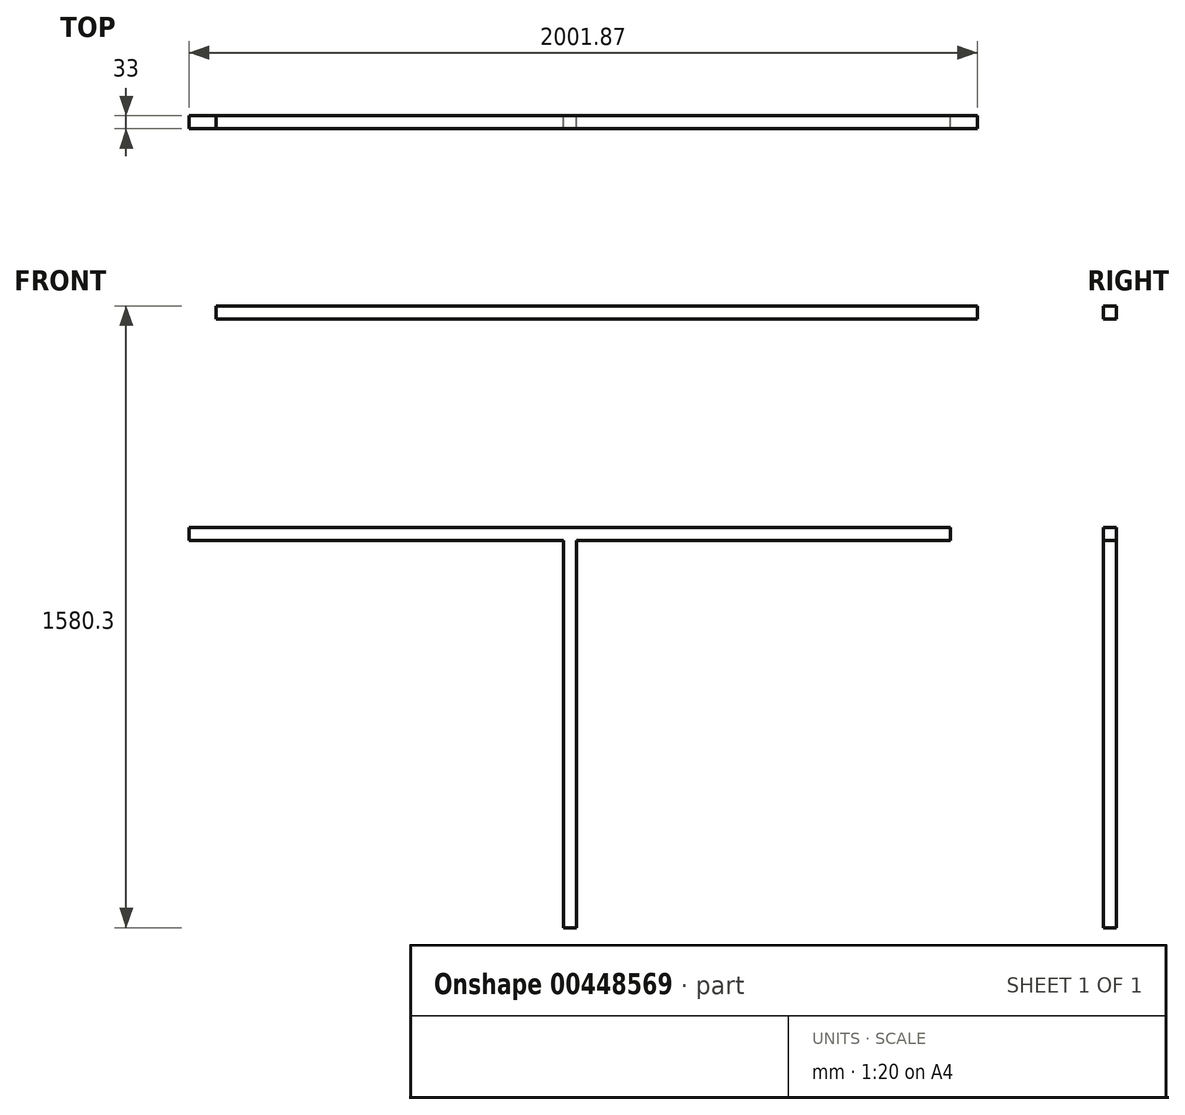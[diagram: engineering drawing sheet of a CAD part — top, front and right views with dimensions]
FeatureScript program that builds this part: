
annotation { "Feature Type Name" : "Feature", "Feature Type Description" : "" }
export const myFeature = defineFeature(function(context is Context, id is Id, definition is map)
    precondition{}
    {
        {
            var Q0;
            Q0=qCreatedBy(makeId("Front.planeOp"),FACE);
            var sketch = newSketch(context, id + "F0", { "sketchPlane" : qUnion([Q0])});
            skLineSegment(sketch, "E0.bottom", {"start": v(983.5, 0) * mm, "end": v(1016.5, 0) * mm});
            skLineSegment(sketch, "E1.0", {"start": v(33, 983.5) * mm, "end": v(33, 1016.5) * mm});
            skLineSegment(sketch, "E1.2", {"start": v(1967, 983.5) * mm, "end": v(1967, 1016.5) * mm});
            skLineSegment(sketch, "E2.right", {"start": v(1016.5, 983.5) * mm, "end": v(1016.5, 0) * mm});
            skLineSegment(sketch, "E3.bottom", {"start": v(33, 1016.5) * mm, "end": v(1967, 1016.5) * mm});
            skLineSegment(sketch, "E3.top", {"start": v(33, 983.5) * mm, "end": v(983.5, 983.5) * mm});
            skLineSegment(sketch, "E3.left", {"start": v(33, 1016.5) * mm, "end": v(33, 983.5) * mm});
            skLineSegment(sketch, "E3.right", {"start": v(1967, 1016.5) * mm, "end": v(1967, 983.5) * mm});
            skLineSegment(sketch, "E4.trimOffspring", {"start": v(983.5, 983.5) * mm, "end": v(983.5, 0) * mm});
            skLineSegment(sketch, "E5.trimOffspring", {"start": v(1016.5, 983.5) * mm, "end": v(1967, 983.5) * mm});
            skLineSegment(sketch, "E6.bottom", {"start": v(100.87, 1580.3) * mm, "end": v(2034.87, 1580.3) * mm});
            skLineSegment(sketch, "E6.top", {"start": v(100.87, 1547.3) * mm, "end": v(2034.87, 1547.3) * mm});
            skLineSegment(sketch, "E6.left", {"start": v(100.87, 1580.3) * mm, "end": v(100.87, 1547.3) * mm});
            skLineSegment(sketch, "E6.right", {"start": v(2034.87, 1580.3) * mm, "end": v(2034.87, 1547.3) * mm});
            skSolve(sketch);
        }
        {
            var Q0;
            Q0=qSketchRegion(id+"F0",true);
            var Q1;
            {var subQ5=sQuery(id+"F0.wireOp",EDGE,"E3.left");Q1=makeQuery(id+"F0.imprint","IMPRINT",FACE,{"disambiguationData":[TD([[makeQuery(id+"F0.imprint","IMPRINT",EDGE,{"derivedFrom":subQ5}),1.0]])]});}
            var Q2;
            {var subQ5=sQuery(id+"F0.wireOp",EDGE,"E3.right");Q2=makeQuery(id+"F0.imprint","IMPRINT",FACE,{"disambiguationData":[TD([[makeQuery(id+"F0.imprint","IMPRINT",EDGE,{"derivedFrom":subQ5}),-1.0]])]});}
            var Q3;
            {var subQ0=sQuery(id+"F0.wireOp",EDGE,"E2.top");Q3=makeQuery(id+"F0.imprint","IMPRINT",FACE,{"disambiguationData":[TD([[makeQuery(id+"F0.imprint","IMPRINT",EDGE,{"derivedFrom":subQ0}),1.0]])]});}
            var Q4;
            {var subQ0=sQuery(id+"F0.wireOp",EDGE,"E3.bottom");var subQ1=sQuery(id+"F0.wireOp",EDGE,"E2.left");var subQ2=makeQuery(id+"F0.imprint","INTERSECT",VERTEX,{"derivedFrom":[subQ1,subQ0]});Q4=makeQuery(id+"F0.imprint","IMPRINT",FACE,{"disambiguationData":[TD([[makeQuery(id+"F0.imprint","IMPRINT",EDGE,{"disambiguationData":[TD([[subQ2,-1.0]])],"derivedFrom":subQ1}),1.0]])]});}
            var Q5;
            {var subQ0=sQuery(id+"F0.wireOp",EDGE,"E2.bottom");Q5=makeQuery(id+"F0.imprint","IMPRINT",FACE,{"disambiguationData":[TD([[makeQuery(id+"F0.imprint","IMPRINT",EDGE,{"derivedFrom":subQ0}),-1.0]])]});}
            extrude(context, id + "F1", {"entities" : qUnion([Q0, Q1, Q2, Q3, Q4, Q5]), "depth" : 33 * mm});
        }
    });
